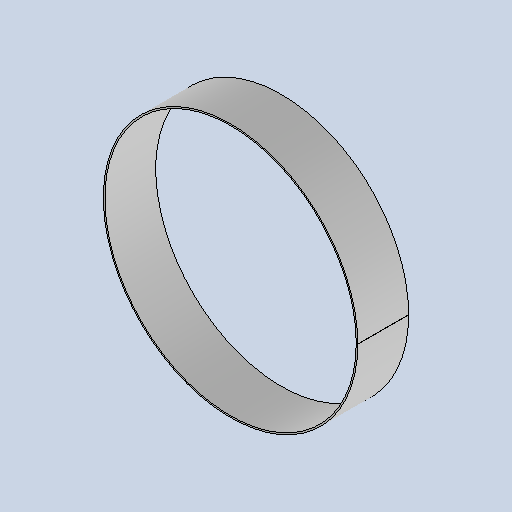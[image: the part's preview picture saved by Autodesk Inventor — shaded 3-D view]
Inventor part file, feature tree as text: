
AUTODESK INVENTOR PART (.ipt)
format: ipt  version: 2025 (Build 290162010, 162A)  size: 278,528 bytes
history: native  units: mm
features: revolve x1, sketch x1, other x1
ambient origin geometry x8: Origin, YZ Plane, XZ Plane, XY Plane, X Axis, Y Axis, Z Axis, Center Point
bodies: Solid1 (feature_tree)
feature tree (3):
  revolve  "Revolution1"  [1 undecoded]
  sketch  "Sketch3"  dims[d1=3.0mm d2=100.0mm d3=250.0mm d4=62.8144mm]
  other  "Definition1"
note: 1 required parameter value undecoded (feature->parameter linkage not recoverable at this tier; creation-order binding heuristic only, values carry confidence <= 0.55)
